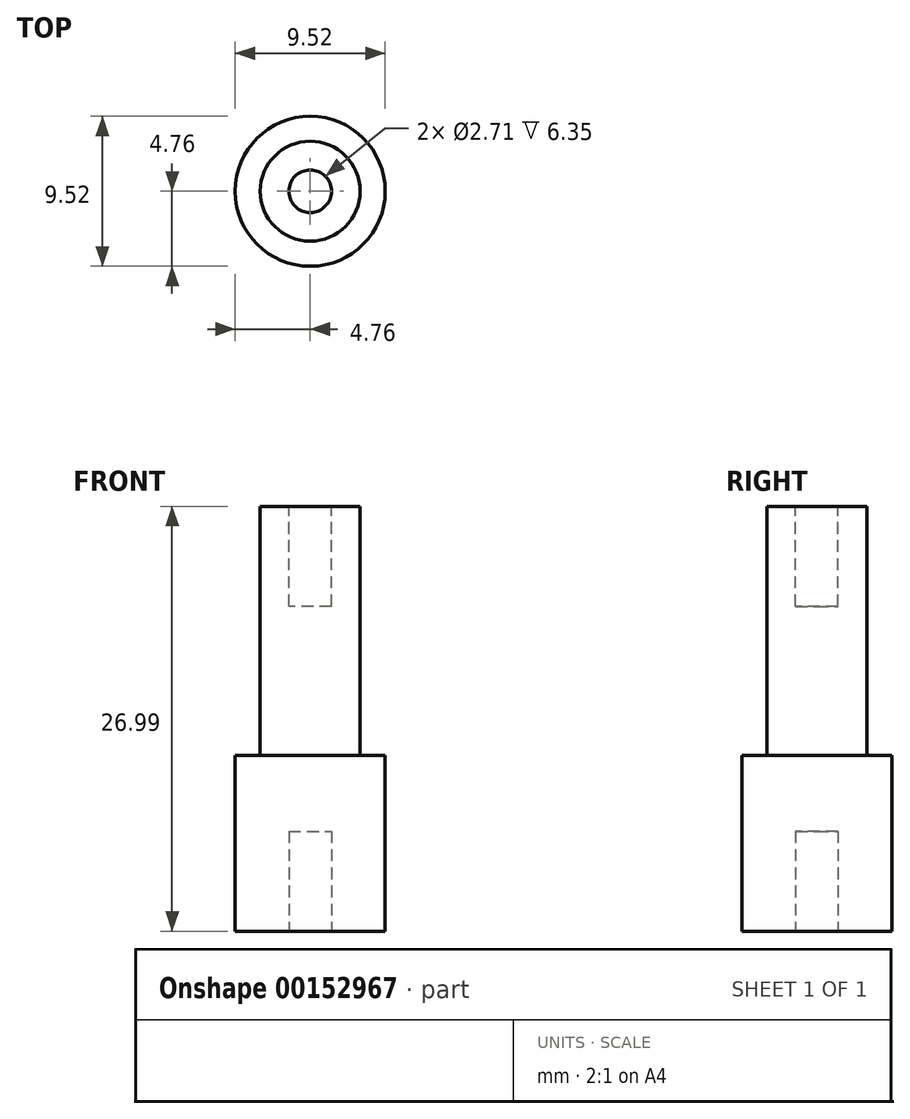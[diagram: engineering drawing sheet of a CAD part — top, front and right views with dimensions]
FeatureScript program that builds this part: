
annotation { "Feature Type Name" : "Feature", "Feature Type Description" : "" }
export const myFeature = defineFeature(function(context is Context, id is Id, definition is map)
    precondition{}
    {
        {
            var Q0;
            Q0=qCreatedBy(makeId("Top.planeOp"),FACE);
            var sketch = newSketch(context, id + "F0", { "sketchPlane" : qUnion([Q0])});
            skCircle(sketch, "E0", {"center": v(0, 0) * mm, "radius": 4.76 * mm});
            skSolve(sketch);
        }
        {
            var Q0;
            Q0 = qSketchRegion(id + "F0", true);
            extrude(context, id + "F1", {"entities" : qUnion([Q0]), "depth" : 11.16 * mm});
        }
        {
            var Q0;
            Q0=makeQuery(id+"F1.opExtrude","CAP_FACE",FACE,{"disambiguationData":[OSD([sQuery(id+"F0.wireOp",EDGE,"E0")])],"isStart":false});
            var sketch = newSketch(context, id + "F2", { "sketchPlane" : qUnion([Q0])});
            skCircle(sketch, "E1", {"center": v(0, 0) * mm, "radius": 3.18 * mm});
            skSolve(sketch);
        }
        {
            var Q0;
            Q0 = qSketchRegion(id + "F2", true);
            extrude(context, id + "F3", {"entities" : qUnion([Q0]), "operationType" : NewBodyOperationType.ADD, "depth" : 15.82 * mm});
        }
        {
            var Q0;
            Q0=makeQuery(id+"F3.opExtrude","CAP_FACE",FACE,{"disambiguationData":[OSD([sQuery(id+"F2.wireOp",EDGE,"E1")])],"isStart":false});
            var sketch = newSketch(context, id + "F4", { "sketchPlane" : qUnion([Q0])});
            skCircle(sketch, "E2", {"center": v(0, 0) * mm, "radius": 1.35 * mm});
            skSolve(sketch);
        }
        {
            var Q0;
            Q0 = qSketchRegion(id + "F4", true);
            extrude(context, id + "F5", {"entities" : qUnion([Q0]), "operationType" : NewBodyOperationType.REMOVE, "oppositeDirection" : true, "depth" : 6.35 * mm});
        }
        {
            var Q0;
            Q0=makeQuery(id+"F1.opExtrude","CAP_FACE",FACE,{"disambiguationData":[OSD([sQuery(id+"F0.wireOp",EDGE,"E0")])],"isStart":true});
            var sketch = newSketch(context, id + "F6", { "sketchPlane" : qUnion([Q0])});
            skCircle(sketch, "E3", {"center": v(0, 0) * mm, "radius": 1.35 * mm});
            skSolve(sketch);
        }
        {
            var Q0;
            Q0 = qSketchRegion(id + "F6", true);
            extrude(context, id + "F7", {"entities" : qUnion([Q0]), "operationType" : NewBodyOperationType.REMOVE, "oppositeDirection" : true, "depth" : 6.35 * mm});
        }
    });
